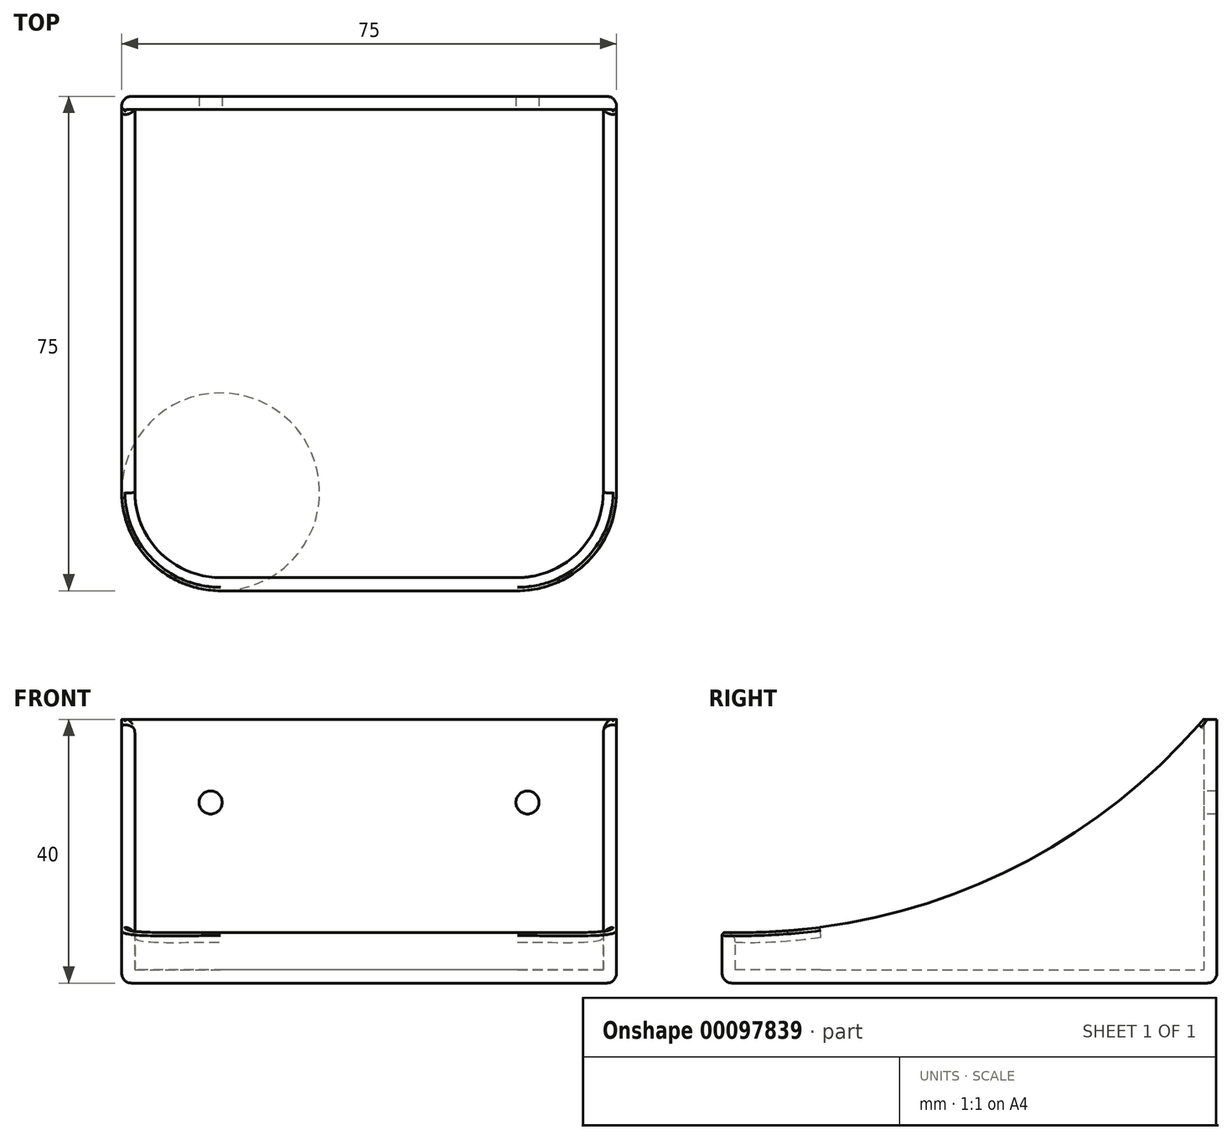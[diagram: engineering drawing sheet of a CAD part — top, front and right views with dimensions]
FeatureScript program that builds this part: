
annotation { "Feature Type Name" : "Feature", "Feature Type Description" : "" }
export const myFeature = defineFeature(function(context is Context, id is Id, definition is map)
    precondition{}
    {
        {
            var Q0;
            Q0=qCreatedBy(makeId("Right.planeOp"),FACE);
            var sketch = newSketch(context, id + "F0", { "sketchPlane" : qUnion([Q0])});
            skLineSegment(sketch, "E0.bottom", {"start": v(-37.5, 20) * mm, "end": v(37.5, 20) * mm});
            skLineSegment(sketch, "E0.top", {"start": v(-37.5, -20) * mm, "end": v(37.5, -20) * mm});
            skLineSegment(sketch, "E0.left", {"start": v(-37.5, 20) * mm, "end": v(-37.5, -20) * mm});
            skLineSegment(sketch, "E0.right", {"start": v(37.5, 20) * mm, "end": v(37.5, -20) * mm});
            skPoint(sketch, "E0.middle", {"position": v(0, 0) * mm});
            skSolve(sketch);
        }
        {
            var Q0;
            Q0 = qSketchRegion(id + "F0", true);
            extrude(context, id + "F1", {"entities" : qUnion([Q0]), "depth" : 75 * mm, "symmetric" : true});
        }
        {
            var Q0;
            Q0=makeQuery(id+"F1.opExtrude","CAP_EDGE",EDGE,{"disambiguationData":[OSD([sQuery(id+"F0.wireOp",EDGE,"E0.left")])],"isStart":true});
            var Q1;
            Q1=makeQuery(id+"F1.opExtrude","CAP_EDGE",EDGE,{"disambiguationData":[OSD([sQuery(id+"F0.wireOp",EDGE,"E0.left")])],"isStart":false});
            fillet(context, id + "F2", {"entities" : qUnion([Q0, Q1]), "radius" : 15 * mm, "tangentPropagation" : true, "allowEdgeOverflow" : false});
        }
        {
            var Q0;
            Q0=makeQuery(id+"F1.opExtrude","SWEPT_FACE",FACE,{"disambiguationData":[OSD([sQuery(id+"F0.wireOp",EDGE,"E0.bottom")])]});
            shell(context, id + "F3", {"entities" : qUnion([Q0]), "thickness" : 2 * mm});
        }
        {
            var Q0;
            Q0=makeQuery(id+"F1.opExtrude","CAP_FACE",FACE,{"disambiguationData":[OSD([sQuery(id+"F0.wireOp",EDGE,"E0.bottom"),sQuery(id+"F0.wireOp",EDGE,"E0.top"),sQuery(id+"F0.wireOp",EDGE,"E0.left"),sQuery(id+"F0.wireOp",EDGE,"E0.right")])],"isStart":false});
            var sketch = newSketch(context, id + "F4", { "sketchPlane" : qUnion([Q0])});
            skLineSegment(sketch, "E1", {"start": v(37.5, 20) * mm, "end": v(35.47, 20) * mm, "construction": true});
            skLineSegment(sketch, "E2", {"start": v(35.47, 20) * mm, "end": v(-37.63, -19.94) * mm, "construction": true});
            skLineSegment(sketch, "E3", {"start": v(-37.63, -19.94) * mm, "end": v(-37.63, -12.24) * mm, "construction": true});
            skSolve(sketch);
        }
        {
            var Q0;
            {var subQ0=sQuery(id+"F0.wireOp",EDGE,"E0.right");Q0=makeQuery(id+"F4.imprint","IMPRINT",FACE,{"disambiguationData":[TD([[makeQuery(id+"F4.imprint","IMPRINT",EDGE,{"derivedFrom":makeQuery(id+"F1.opExtrude","CAP_EDGE",EDGE,{"disambiguationData":[OSD([subQ0])],"isStart":false})}),-1.0]])]});}
            var sketch = newSketch(context, id + "F5", { "sketchPlane" : qUnion([Q0])});
            skArc(sketch, "E4", {"start": v(-37.6, -12.3) * mm, "mid": v(2.6, -4.47) * mm, "end": v(35.45, 19.99) * mm});
            skLineSegment(sketch, "E5", {"start": v(-37.6, -12.3) * mm, "end": v(-37.6, 20.13) * mm});
            skLineSegment(sketch, "E6", {"start": v(-37.6, 20.13) * mm, "end": v(35.45, 19.99) * mm});
            skSolve(sketch);
        }
        {
            var Q0;
            Q0 = qSketchRegion(id + "F5", true);
            extrude(context, id + "F6", {"entities" : qUnion([Q0]), "operationType" : NewBodyOperationType.REMOVE, "oppositeDirection" : true, "depth" : 80 * mm});
        }
        {
            var Q0;
            {var subQ0=sQuery(id+"F0.wireOp",EDGE,"E0.right");Q0=makeQuery(id+"F4.imprint","IMPRINT",FACE,{"disambiguationData":[TD([[makeQuery(id+"F4.imprint","IMPRINT",EDGE,{"derivedFrom":makeQuery(id+"F1.opExtrude","CAP_EDGE",EDGE,{"disambiguationData":[OSD([subQ0])],"isStart":false})}),-1.0]])]});}
            var sketch = newSketch(context, id + "F7", { "sketchPlane" : qUnion([Q0])});
            skEllipse(sketch, "E7", {"center": v(29.37, 20) * mm, "majorRadius": 7.56 * mm, "minorRadius": 3.85 * mm, "majorAxis": v(0.9, 0.44)});
            skSolve(sketch);
        }
        {
            var Q0;
            Q0 = qSketchRegion(id + "F7", true);
            extrude(context, id + "F8", {"entities" : qUnion([Q0]), "operationType" : NewBodyOperationType.REMOVE, "oppositeDirection" : true, "depth" : 75 * mm});
        }
        {
            var Q0;
            {var subQ0=sQuery(id+"F0.wireOp",EDGE,"E0.left");var subQ1=sQuery(id+"F0.wireOp",EDGE,"E0.right");var subQ2=sQuery(id+"F0.wireOp",EDGE,"E0.top");var subQ3=sQuery(id+"F0.wireOp",EDGE,"E0.bottom");var subQ4=makeQuery(id+"F3.opShell","OFFSET_FACE",FACE,{"disambiguationData":[OSD([subQ3,subQ2,subQ0,subQ1]),TDD([makeQuery(id+"F1.opExtrude","CAP_FACE",FACE,{"disambiguationData":[OSD([subQ3,subQ2,subQ0,subQ1])],"isStart":true})])]});var subQ5=makeQuery(id+"F6.opExtrude","SWEPT_FACE",FACE,{"disambiguationData":[OSD([sQuery(id+"F5.wireOp",EDGE,"E4")])]});Q0=makeQuery(id+"F8.boolean.opBoolean","SPLIT",EDGE,{"disambiguationData":[TD([makeQuery(id+"F3.opShell","OFFSET_FACE",FACE,{"disambiguationData":[OSD([subQ0]),TDD([makeQuery(id+"F2.opFillet","BLEND_FACE",FACE,{"disambiguationData":[OSD([subQ0]),TDD([makeQuery(id+"F1.opExtrude","CAP_EDGE",EDGE,{"disambiguationData":[OSD([subQ0])],"isStart":true})])]})])]})])],"derivedFrom":makeQuery(id+"F6.boolean.opBoolean","INTERSECT",EDGE,{"derivedFrom":[subQ4,subQ5]})});}
            var Q1;
            Q1=makeQuery(id+"F1.opExtrude","CAP_EDGE",EDGE,{"disambiguationData":[OSD([sQuery(id+"F0.wireOp",EDGE,"E0.right")])],"isStart":false});
            var Q2;
            Q2=makeQuery(id+"F1.opExtrude","CAP_EDGE",EDGE,{"disambiguationData":[OSD([sQuery(id+"F0.wireOp",EDGE,"E0.top")])],"isStart":false});
            var Q3;
            Q3=makeQuery(id+"F1.opExtrude","SWEPT_EDGE",EDGE,{"disambiguationData":[OSD([sQuery(id+"F0.wireOp",EDGE,"E0.top"),sQuery(id+"F0.wireOp",EDGE,"E0.right")])]});
            var Q4;
            Q4=makeQuery(id+"F1.opExtrude","CAP_EDGE",EDGE,{"disambiguationData":[OSD([sQuery(id+"F0.wireOp",EDGE,"E0.right")])],"isStart":true});
            fillet(context, id + "F9", {"entities" : qUnion([Q0, Q1, Q2, Q3, Q4]), "radius" : 1.5 * mm, "tangentPropagation" : true, "allowEdgeOverflow" : false});
        }
        {
            var Q0;
            {var subQ0=sQuery(id+"F0.wireOp",EDGE,"E0.left");var subQ1=makeQuery(id+"F1.opExtrude","CAP_FACE",FACE,{"disambiguationData":[OSD([sQuery(id+"F0.wireOp",EDGE,"E0.bottom"),sQuery(id+"F0.wireOp",EDGE,"E0.top"),subQ0,sQuery(id+"F0.wireOp",EDGE,"E0.right")])],"isStart":true});var subQ2=makeQuery(id+"F6.opExtrude","SWEPT_FACE",FACE,{"disambiguationData":[OSD([sQuery(id+"F5.wireOp",EDGE,"E4")])]});Q0=makeQuery(id+"F8.boolean.opBoolean","SPLIT",EDGE,{"disambiguationData":[TD([makeQuery(id+"F2.opFillet","BLEND_FACE",FACE,{"disambiguationData":[OSD([subQ0]),TDD([makeQuery(id+"F1.opExtrude","CAP_EDGE",EDGE,{"disambiguationData":[OSD([subQ0])],"isStart":true})])]})])],"derivedFrom":makeQuery(id+"F6.boolean.opBoolean","INTERSECT",EDGE,{"derivedFrom":[subQ1,subQ2]})});}
            fillet(context, id + "F10", {"entities" : qUnion([Q0]), "radius" : .5 * mm, "tangentPropagation" : true, "allowEdgeOverflow" : false});
        }
        {
            var Q0;
            Q0=makeQuery(id+"F1.opExtrude","SWEPT_FACE",FACE,{"disambiguationData":[OSD([sQuery(id+"F0.wireOp",EDGE,"E0.right")])]});
            var sketch = newSketch(context, id + "F11", { "sketchPlane" : qUnion([Q0])});
            skLineSegment(sketch, "E8", {"start": v(-12.03, 7.4) * mm, "end": v(-36, 7.4) * mm, "construction": true});
            skLineSegment(sketch, "E9", {"start": v(-36, 7.4) * mm, "end": v(36, 7.4) * mm, "construction": true});
            skLineSegment(sketch, "E10.bottom", {"start": v(-24.01, 7.4) * mm, "end": v(24.01, 7.4) * mm, "construction": true});
            skLineSegment(sketch, "E10.top", {"start": v(-24.01, -7.4) * mm, "end": v(24.01, -7.4) * mm, "construction": true});
            skLineSegment(sketch, "E10.left", {"start": v(-24.01, 7.4) * mm, "end": v(-24.01, -7.4) * mm, "construction": true});
            skLineSegment(sketch, "E10.right", {"start": v(24.01, 7.4) * mm, "end": v(24.01, -7.4) * mm, "construction": true});
            skPoint(sketch, "E10.middle", {"position": v(0, 0) * mm});
            skSolve(sketch);
        }
        {
            var Q0;
            Q0=sQuery(id+"F11.wireOp",VERTEX,"E10.left.start");
            var Q1;
            Q1=sQuery(id+"F11.wireOp",VERTEX,"E10.bottom.end");
            var Q2;
            Q2=makeQuery(id+"F1.opExtrude","SWEPT_BODY",BODY,{"disambiguationData":[OSD([sQuery(id+"F0.wireOp",EDGE,"E0.bottom"),sQuery(id+"F0.wireOp",EDGE,"E0.top"),sQuery(id+"F0.wireOp",EDGE,"E0.left"),sQuery(id+"F0.wireOp",EDGE,"E0.right")])]});
            hole(context, id + "F12", {"style" : HoleStyle.SIMPLE, "endStyle" : HoleEndStyle.THROUGH, "holeDiameter" : 3.5 * mm, "locations" : qUnion([Q0, Q1]), "scope" : qUnion([Q2]), "isTappedThrough" : true});
        }
    });
